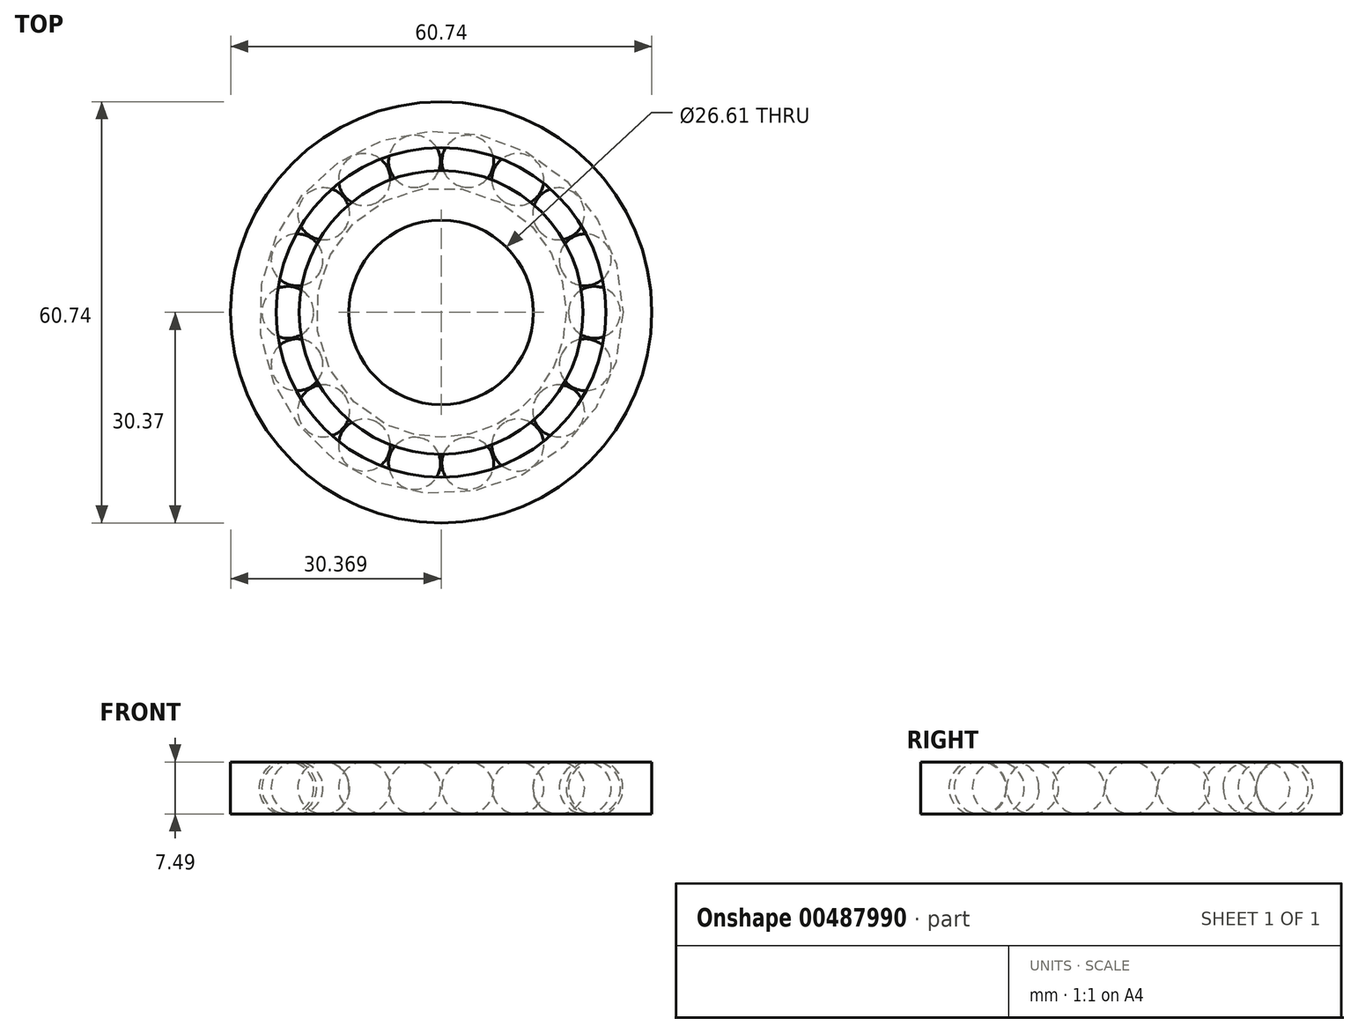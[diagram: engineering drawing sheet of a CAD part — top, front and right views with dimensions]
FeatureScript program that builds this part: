
annotation { "Feature Type Name" : "Feature", "Feature Type Description" : "" }
export const myFeature = defineFeature(function(context is Context, id is Id, definition is map)
    precondition{}
    {
        {
            var Q0;
            Q0=qCreatedBy(makeId("Front.planeOp"),FACE);
            var sketch = newSketch(context, id + "F0", { "sketchPlane" : qUnion([Q0])});
            skLineSegment(sketch, "E0", {"start": v(0, 0) * mm, "end": v(0, 45.76) * mm});
            skLineSegment(sketch, "E1", {"start": v(-55.3, 25.47) * mm, "end": v(-55.3, 17.98) * mm});
            skPoint(sketch, "E2.1.internal.snap0", {"position": v(-55.3, 21.73) * mm});
            skCircle(sketch, "E3", {"center": v(-47.04, 21.73) * mm, "radius": 3.75 * mm});
            skLineSegment(sketch, "E4", {"start": v(-50.13, 25.47) * mm, "end": v(-55.3, 25.47) * mm});
            skLineSegment(sketch, "E5", {"start": v(-50.04, 17.98) * mm, "end": v(-55.3, 17.98) * mm});
            skLineSegment(sketch, "E6", {"start": v(-38.23, 17.98) * mm, "end": v(-38.23, 25.47) * mm});
            skLineSegment(sketch, "E7", {"start": v(-47.04, 25.47) * mm, "end": v(-47.04, 17.98) * mm});
            skArc(sketch, "E8", {"start": v(-45.39, 17.98) * mm, "mid": v(-42.94, 21.73) * mm, "end": v(-45.39, 25.47) * mm});
            skLineSegment(sketch, "E9", {"start": v(-55.3, 17.98) * mm, "end": v(-48.7, 17.98) * mm});
            skLineSegment(sketch, "E10", {"start": v(-55.3, 25.47) * mm, "end": v(-48.7, 25.47) * mm});
            skLineSegment(sketch, "E11", {"start": v(-38.23, 17.98) * mm, "end": v(-45.39, 17.98) * mm});
            skLineSegment(sketch, "E12", {"start": v(-38.23, 25.47) * mm, "end": v(-45.39, 25.47) * mm});
            skArc(sketch, "E13.trimOffspring", {"start": v(-48.7, 25.47) * mm, "mid": v(-51.13, 21.73) * mm, "end": v(-48.7, 17.98) * mm});
            skLineSegment(sketch, "E14", {"start": v(-24.92, 25.47) * mm, "end": v(-24.92, 17.98) * mm});
            skSolve(sketch);
        }
        {
            var Q0;
            Q0=makeQuery(id+"F0.imprint","IMPRINT",FACE,{"disambiguationData":[TD([[makeQuery(id+"F0.imprint","IMPRINT",EDGE,{"derivedFrom":sQuery(id+"F0.wireOp",EDGE,"E1")}),1.0]])]});
            var Q1;
            Q1=makeQuery(id+"F0.imprint","IMPRINT",FACE,{"disambiguationData":[TD([[makeQuery(id+"F0.imprint","IMPRINT",EDGE,{"derivedFrom":sQuery(id+"F0.wireOp",EDGE,"E6")}),1.0]])]});
            var Q2;
            Q2=sQuery(id+"F0.wireOp",EDGE,"E14");
            revolve(context, id + "F1", {"entities" : qUnion([Q0, Q1]), "axis" : qUnion([Q2]), "revolveType" : RevolveType.FULL});
        }
        {
            var Q0;
            {var subQ0=sQuery(id+"F0.wireOp",EDGE,"E7");Q0=makeQuery(id+"F0.imprint","IMPRINT",FACE,{"disambiguationData":[TD([[makeQuery(id+"F0.imprint","IMPRINT",EDGE,{"derivedFrom":subQ0}),1.0]])]});}
            var Q1;
            Q1=sQuery(id+"F0.wireOp",EDGE,"E7");
            revolve(context, id + "F2", {"entities" : qUnion([Q0]), "axis" : qUnion([Q1]), "revolveType" : RevolveType.FULL});
        }
        {
            var Q0;
            Q0=makeQuery(id+"F2.opRevolve","SWEPT_BODY",BODY,{"disambiguationData":[OSD([sQuery(id+"F0.wireOp",EDGE,"E3"),sQuery(id+"F0.wireOp",EDGE,"E7")])]});
            var Q1;
            Q1=sQuery(id+"F0.wireOp",EDGE,"E14");
            circularPattern(context, id + "F3", {"entities" : qUnion([Q0]), "axis" : qUnion([Q1]), "angle" : 360 * degree, "instanceCount" : 18, "equalSpace" : true});
        }
        {
            var Q0;
            Q0=makeQuery(id+"F1.opRevolve","SWEPT_EDGE",EDGE,{"disambiguationData":[OSD([sQuery(id+"F0.wireOp",EDGE,"E1"),sQuery(id+"F0.wireOp",EDGE,"E10")])]});
            var Q1;
            Q1=makeQuery(id+"F1.opRevolve","SWEPT_EDGE",EDGE,{"disambiguationData":[OSD([sQuery(id+"F0.wireOp",EDGE,"E1"),sQuery(id+"F0.wireOp",EDGE,"E9")])]});
            var Q2;
            Q2=makeQuery(id+"F1.opRevolve","SWEPT_EDGE",EDGE,{"disambiguationData":[OSD([sQuery(id+"F0.wireOp",EDGE,"E6"),sQuery(id+"F0.wireOp",EDGE,"E11")])]});
            var Q3;
            Q3=makeQuery(id+"F1.opRevolve","SWEPT_EDGE",EDGE,{"disambiguationData":[OSD([sQuery(id+"F0.wireOp",EDGE,"E6"),sQuery(id+"F0.wireOp",EDGE,"E12")])]});
            fillet(context, id + "F4", {"entities" : qUnion([Q0, Q1, Q2, Q3]), "radius" : 3.56 * mm, "tangentPropagation" : true, "allowEdgeOverflow" : false});
        }
    });
